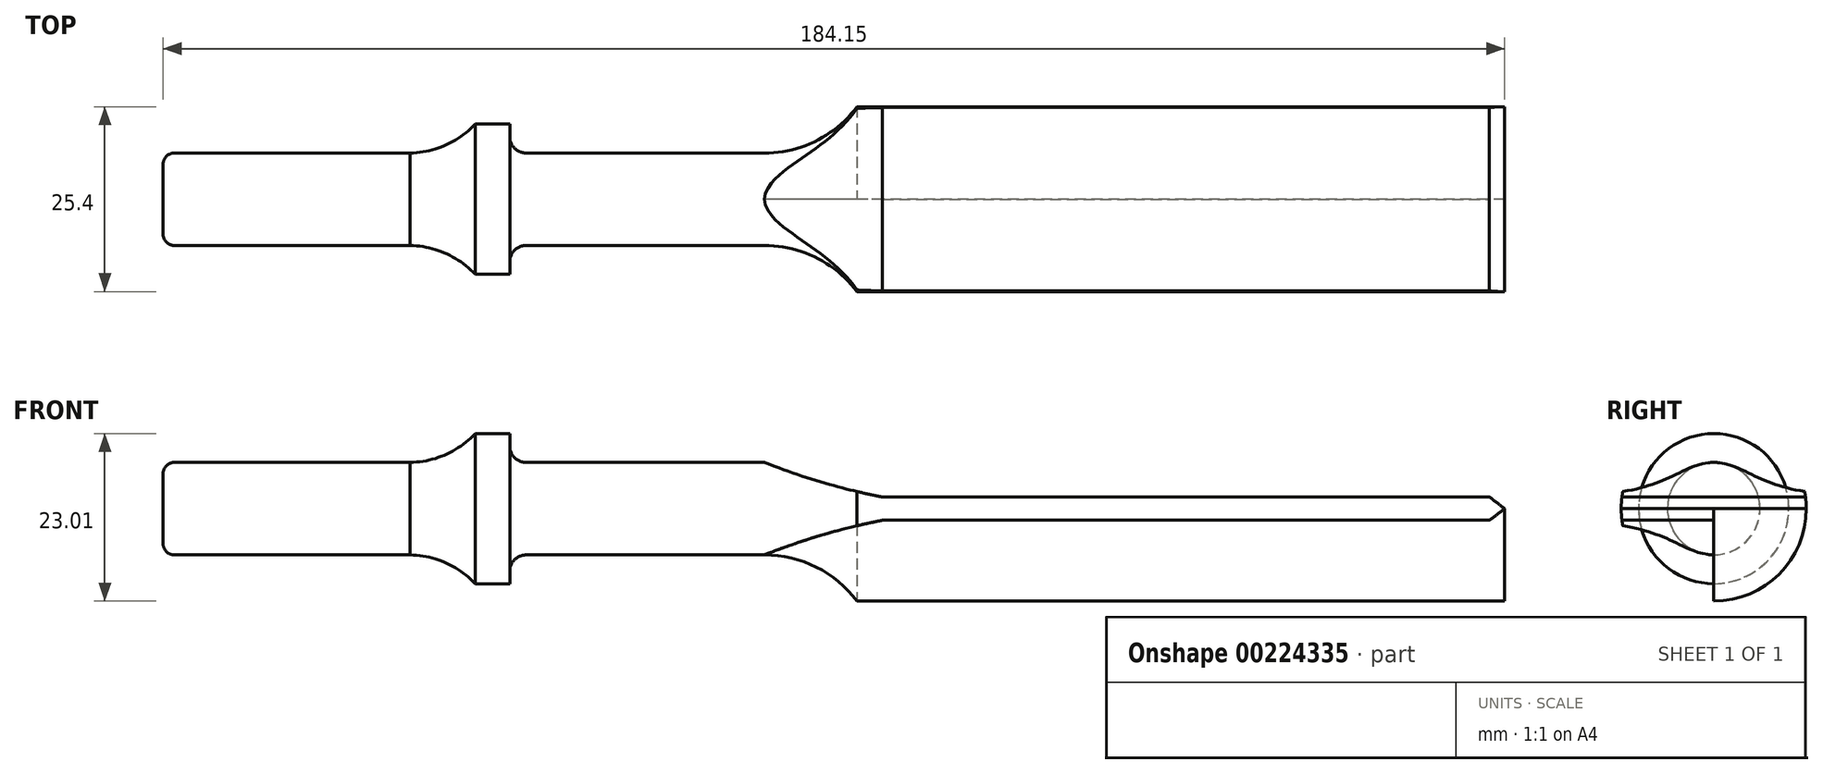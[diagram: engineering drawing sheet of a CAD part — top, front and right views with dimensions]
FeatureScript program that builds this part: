
annotation { "Feature Type Name" : "Feature", "Feature Type Description" : "" }
export const myFeature = defineFeature(function(context is Context, id is Id, definition is map)
    precondition{}
    {
        {
            var Q0;
            Q0=qCreatedBy(makeId("Front.planeOp"),FACE);
            var sketch = newSketch(context, id + "F0", { "sketchPlane" : qUnion([Q0])});
            skLineSegment(sketch, "E0", {"start": v(0, 0) * mm, "end": v(184.15, 0) * mm});
            skLineSegment(sketch, "E1", {"start": v(184.15, 0) * mm, "end": v(184.15, 12.7) * mm});
            skLineSegment(sketch, "E2", {"start": v(0, 0) * mm, "end": v(0, 4.83) * mm});
            skLineSegment(sketch, "E3", {"start": v(1.52, 6.35) * mm, "end": v(33.92, 6.35) * mm});
            skLineSegment(sketch, "E4", {"start": v(42.85, 10.3) * mm, "end": v(47.6, 10.3) * mm});
            skLineSegment(sketch, "E5", {"start": v(47.6, 10.3) * mm, "end": v(47.56, 8.7) * mm});
            skLineSegment(sketch, "E6.0", {"start": v(82.55, 0) * mm, "end": v(82.55, 12.7) * mm, "construction": true});
            skLineSegment(sketch, "E7.0", {"start": v(95.25, 0) * mm, "end": v(95.25, 12.7) * mm, "construction": true});
            skLineSegment(sketch, "E8", {"start": v(184.15, 12.7) * mm, "end": v(82.55, 12.7) * mm});
            skLineSegment(sketch, "E9.trimOffspring", {"start": v(49.84, 6.35) * mm, "end": v(82.55, 6.35) * mm});
            skArc(sketch, "E10", {"start": v(82.55, 6.35) * mm, "mid": v(89.65, 8.03) * mm, "end": v(95.25, 12.7) * mm});
            skArc(sketch, "E11", {"start": v(33.63, 6.35) * mm, "mid": v(38.65, 7.38) * mm, "end": v(42.85, 10.3) * mm});
            skPoint(sketch, "E12.visualSharp", {"position": v(0, 6.35) * mm});
            skArc(sketch, "E12.filletArc", {"start": v(1.52, 6.35) * mm, "mid": v(0.45, 5.9) * mm, "end": v(0, 4.83) * mm});
            skPoint(sketch, "E13.visualSharp", {"position": v(47.5, 6.35) * mm});
            skArc(sketch, "E13.filletArc", {"start": v(47.56, 8.7) * mm, "mid": v(48.2, 7.04) * mm, "end": v(49.84, 6.35) * mm});
            skSolve(sketch);
        }
        {
            var Q0;
            Q0=makeQuery(id+"F0.imprint","IMPRINT",FACE,{"disambiguationData":[TD([[makeQuery(id+"F0.imprint","IMPRINT",EDGE,{"derivedFrom":sQuery(id+"F0.wireOp",EDGE,"E0")}),1.0]])]});
            var Q1;
            Q1=sQuery(id+"F0.wireOp",EDGE,"E0");
            revolve(context, id + "F1", {"entities" : qUnion([Q0]), "axis" : qUnion([Q1]), "revolveType" : RevolveType.FULL});
        }
        {
            var Q0;
            Q0=qCreatedBy(makeId("Front.planeOp"),FACE);
            var sketch = newSketch(context, id + "F2", { "sketchPlane" : qUnion([Q0])});
            skLineSegment(sketch, "E14", {"start": v(184.15, 1.6) * mm, "end": v(184.15, 27.94) * mm, "construction": true});
            skLineSegment(sketch, "E15.0", {"start": v(82.55, 6.35) * mm, "end": v(82.55, 27.94) * mm, "construction": true});
            skLineSegment(sketch, "E16.0", {"start": v(0, 6.35) * mm, "end": v(82.55, 6.35) * mm});
            skPoint(sketch, "E17", {"position": v(82.55, 6.35) * mm});
            skLineSegment(sketch, "E18.0", {"start": v(98.75, 1.6) * mm, "end": v(182.06, 1.6) * mm});
            skArc(sketch, "E19", {"start": v(82.55, 6.35) * mm, "mid": v(90.54, 3.59) * mm, "end": v(98.75, 1.6) * mm});
            skLineSegment(sketch, "E20", {"start": v(184.15, 0) * mm, "end": v(184.15, 1.6) * mm});
            skLineSegment(sketch, "E21", {"start": v(82.55, 6.35) * mm, "end": v(82.55, 42.2) * mm});
            skLineSegment(sketch, "E22", {"start": v(82.55, 42.2) * mm, "end": v(196.6, 42.2) * mm});
            skLineSegment(sketch, "E23", {"start": v(184.15, 0) * mm, "end": v(182.06, 1.6) * mm});
            skLineSegment(sketch, "E24", {"start": v(196.6, 42.2) * mm, "end": v(184.15, 0) * mm});
            skLineSegment(sketch, "E25.MirrorCS", {"start": v(82.55, 0) * mm, "end": v(82.55, -1.6) * mm});
            skLineSegment(sketch, "E26", {"start": v(0, 0) * mm, "end": v(218.7, 0) * mm, "construction": true});
            skArc(sketch, "E27.MirrorCS", {"start": v(82.55, -6.35) * mm, "mid": v(90.54, -3.59) * mm, "end": v(98.75, -1.6) * mm});
            skLineSegment(sketch, "E28.MirrorCS", {"start": v(82.55, -42.2) * mm, "end": v(196.6, -42.2) * mm});
            skLineSegment(sketch, "E29.MirrorCS", {"start": v(196.6, -42.2) * mm, "end": v(184.15, 0) * mm});
            skLineSegment(sketch, "E30", {"start": v(82.55, -42.2) * mm, "end": v(82.55, -27.94) * mm});
            skLineSegment(sketch, "E31.MirrorCS", {"start": v(184.15, 0) * mm, "end": v(182.06, -1.6) * mm});
            skLineSegment(sketch, "E32.MirrorCS", {"start": v(98.75, -1.6) * mm, "end": v(182.06, -1.6) * mm});
            skPoint(sketch, "E33.orphan", {"position": v(179.44, -3.61) * mm});
            skPoint(sketch, "E34.orphan", {"position": v(179.44, 3.61) * mm});
            skPoint(sketch, "E35.orphan", {"position": v(82.55, 1.6) * mm});
            skPoint(sketch, "E36.orphan", {"position": v(115.55, 0) * mm});
            skPoint(sketch, "E37.orphan", {"position": v(82.55, -1.6) * mm});
            skLineSegment(sketch, "E38.trimOffspring", {"start": v(82.55, -6.35) * mm, "end": v(82.55, -27.94) * mm});
            skSolve(sketch);
        }
        {
            var Q0;
            {var subQ0=sQuery(id+"F2.wireOp",EDGE,"E21");Q0=makeQuery(id+"F2.imprint","IMPRINT",FACE,{"disambiguationData":[TD([[makeQuery(id+"F2.imprint","IMPRINT",EDGE,{"derivedFrom":subQ0}),-1.0]])]});}
            var Q1;
            {var subQ2=sQuery(id+"F2.wireOp",EDGE,"E27.MirrorCS");Q1=makeQuery(id+"F2.imprint","IMPRINT",FACE,{"disambiguationData":[TD([[makeQuery(id+"F2.imprint","IMPRINT",EDGE,{"derivedFrom":subQ2}),-1.0]])]});}
            extrude(context, id + "F3", {"entities" : qUnion([Q0, Q1]), "operationType" : NewBodyOperationType.REMOVE, "oppositeDirection" : true, "depth" : 25.4 * mm});
        }
        {
            var Q0;
            Q0 = qSketchRegion(id + "F2", true);
            extrude(context, id + "F4", {"entities" : qUnion([Q0]), "operationType" : NewBodyOperationType.REMOVE, "depth" : 25.4 * mm});
        }
    });
